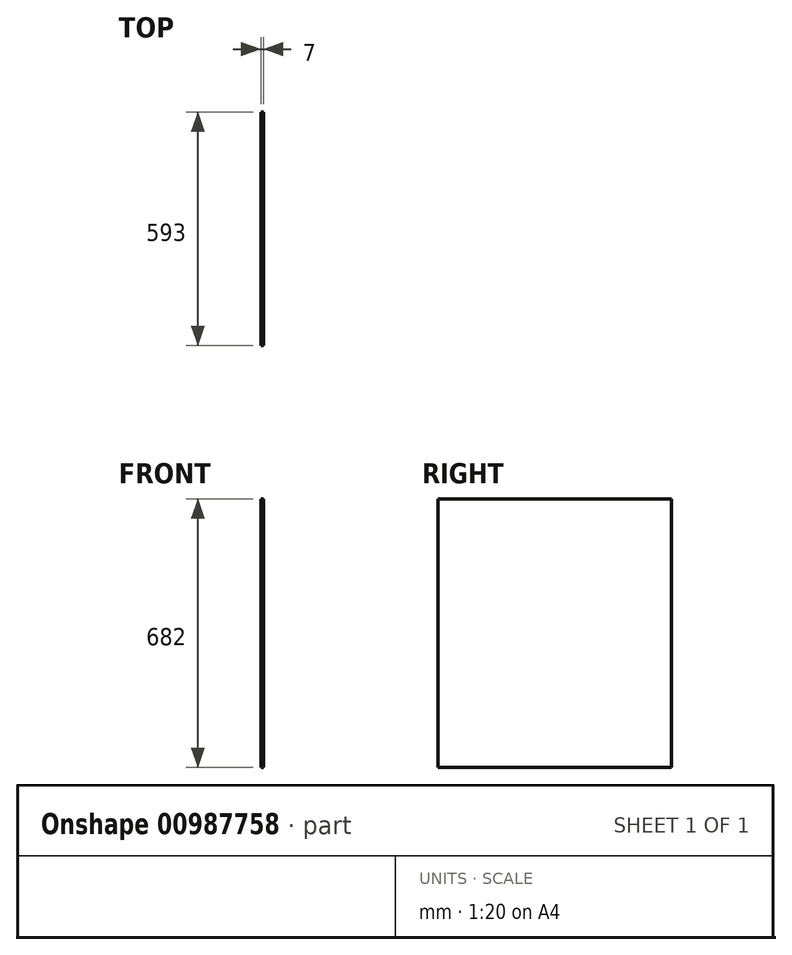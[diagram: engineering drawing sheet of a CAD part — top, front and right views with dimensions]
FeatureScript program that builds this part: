
annotation { "Feature Type Name" : "Feature", "Feature Type Description" : "" }
export const myFeature = defineFeature(function(context is Context, id is Id, definition is map)
    precondition{}
    {
        {
            var Q0;
            Q0=qCreatedBy(makeId("Right.planeOp"),FACE);
            var sketch = newSketch(context, id + "F0", { "sketchPlane" : qUnion([Q0])});
            skLineSegment(sketch, "E0.bottom", {"start": v(-296.5, -341) * mm, "end": v(296.5, -341) * mm});
            skLineSegment(sketch, "E0.top", {"start": v(-296.5, 341) * mm, "end": v(296.5, 341) * mm});
            skLineSegment(sketch, "E0.left", {"start": v(-296.5, -341) * mm, "end": v(-296.5, 341) * mm});
            skLineSegment(sketch, "E0.right", {"start": v(296.5, -341) * mm, "end": v(296.5, 341) * mm});
            skPoint(sketch, "E0.middle", {"position": v(0, 0) * mm});
            skSolve(sketch);
        }
        {
            var Q0;
            Q0=makeQuery(id+"F0.imprint","IMPRINT",FACE,{"disambiguationData":[TD([[makeQuery(id+"F0.imprint","IMPRINT",EDGE,{"derivedFrom":sQuery(id+"F0.wireOp",EDGE,"E0.bottom")}),1.0]])]});
            extrude(context, id + "F1", {"entities" : qUnion([Q0]), "depth" : 7 * mm, "offsetDistance" : 25 * mm});
        }
    });
